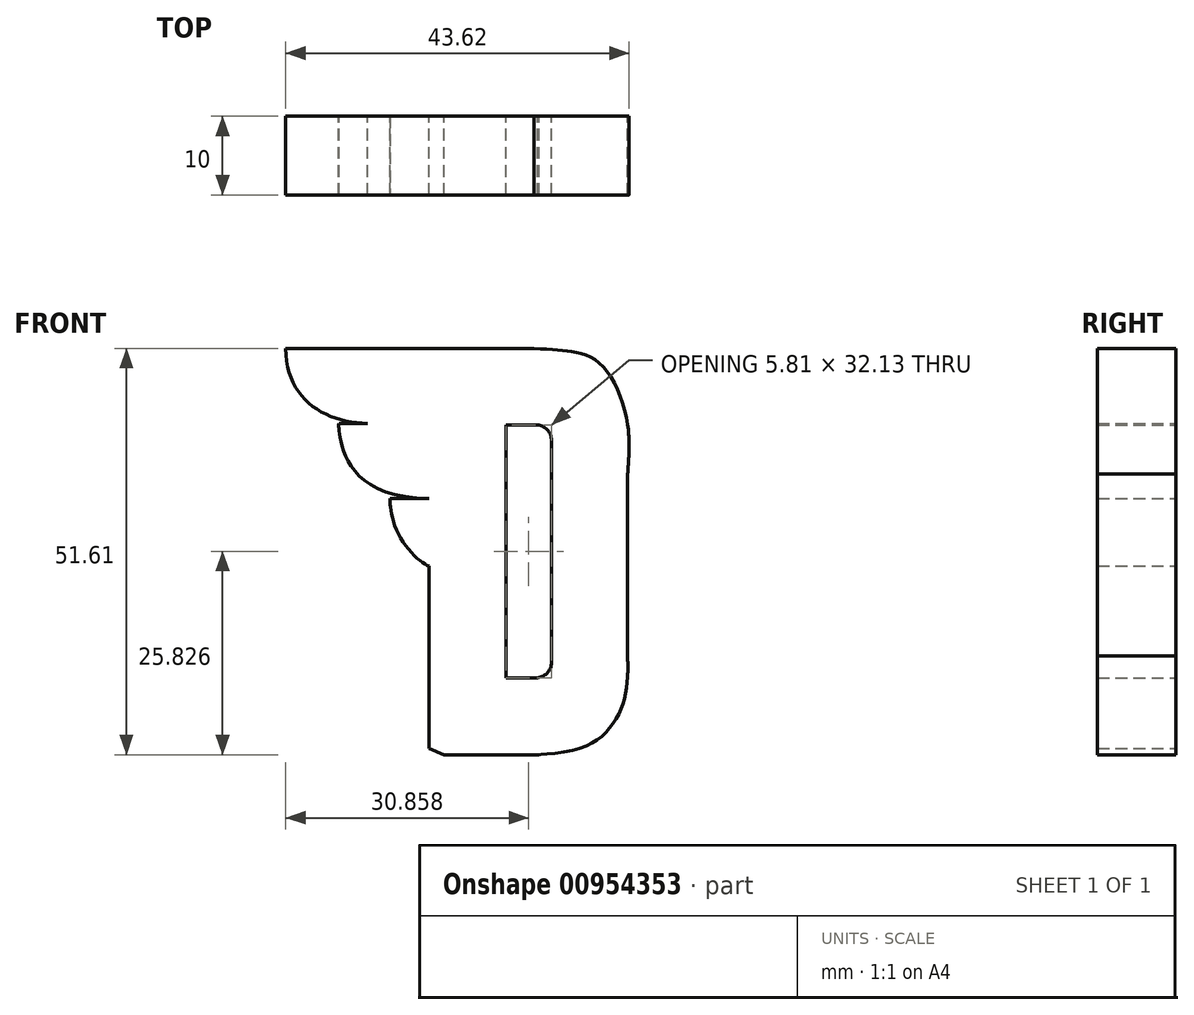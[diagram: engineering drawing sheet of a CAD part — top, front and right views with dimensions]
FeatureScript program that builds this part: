
annotation { "Feature Type Name" : "Feature", "Feature Type Description" : "" }
export const myFeature = defineFeature(function(context is Context, id is Id, definition is map)
    precondition{}
    {
        {
            var Q0;
            Q0=qCreatedBy(makeId("Front.planeOp"),FACE);
            var sketch = newSketch(context, id + "F0", { "sketchPlane" : qUnion([Q0])});
            skLineSegment(sketch, "E0", {"start": v(-33.11, 39.73) * mm, "end": v(-1.57, 39.73) * mm});
            skLineSegment(sketch, "E1", {"start": v(10.32, 30.06) * mm, "end": v(10.32, -2) * mm});
            skFitSpline(sketch, "E2", {"points": [v(-1.57, 39.73) * mm, v(3.32, 39.32) * mm, v(7.13, 37.5) * mm, v(10.32, 30.06) * mm, v(10.32, 23.8) * mm], "startDerivative": vector(27.64, -1.84) * mm, "endDerivative": vector(-1.43, -19.7) * mm});
            skLineSegment(sketch, "E3", {"start": v(-14.92, -11.09) * mm, "end": v(-13.02, -11.88) * mm});
            skLineSegment(sketch, "E4", {"start": v(-13.02, -11.88) * mm, "end": v(-0.96, -11.88) * mm});
            skFitSpline(sketch, "E5", {"points": [v(-0.96, -11.88) * mm, v(2.62, -11.5) * mm, v(7.54, -9.07) * mm, v(9.61, -5.77) * mm, v(10.32, -2) * mm, v(10.32, 0.66) * mm, v(10.32, 0.83) * mm], "startDerivative": vector(-13.72, 0) * mm, "endDerivative": vector(0.1, 2.52) * mm});
            skLineSegment(sketch, "E6", {"start": v(-14.92, -11.09) * mm, "end": v(-14.92, 12.1) * mm});
            skLineSegment(sketch, "E7", {"start": v(-14.9, 20.67) * mm, "end": v(-19.85, 20.67) * mm});
            skLineSegment(sketch, "E8", {"start": v(-22.7, 30.2) * mm, "end": v(-26.36, 30.2) * mm});
            skFitSpline(sketch, "E9", {"points": [v(-14.92, 12.1) * mm, v(-16.37, 13.04) * mm, v(-18.95, 16.47) * mm, v(-19.8, 19.67) * mm, v(-19.85, 20.67) * mm], "startDerivative": vector(-4.8, 1.49) * mm, "endDerivative": vector(0.82, 3.63) * mm});
            skFitSpline(sketch, "E10", {"points": [v(-26.36, 30.2) * mm, v(-26.36, 29.56) * mm, v(-14.9, 20.67) * mm], "startDerivative": vector(-1.22, -3.12) * mm, "endDerivative": vector(38.91, 0) * mm});
            skFitSpline(sketch, "E11", {"points": [v(-33.11, 39.73) * mm, v(-22.73, 30.2) * mm, v(-22.7, 30.2) * mm], "startDerivative": vector(0.13, -20.19) * mm, "endDerivative": vector(-32.01, 0) * mm});
            skLineSegment(sketch, "E12.bottom", {"start": v(-5.16, -2.12) * mm, "end": v(0.65, -2.12) * mm});
            skLineSegment(sketch, "E12.top", {"start": v(-5.16, 30.01) * mm, "end": v(0.65, 30.01) * mm});
            skLineSegment(sketch, "E12.left", {"start": v(-5.16, -2.12) * mm, "end": v(-5.16, 30.01) * mm});
            skLineSegment(sketch, "E12.right", {"start": v(0.65, -2.12) * mm, "end": v(0.65, 30.01) * mm});
            skSolve(sketch);
        }
        {
            var Q0;
            Q0 = qSketchRegion(id + "F0", true);
            extrude(context, id + "F1", {"entities" : qUnion([Q0]), "depth" : 10 * mm, "offsetDistance" : 25 * mm});
        }
        {
            var Q0;
            Q0=makeQuery(id+"F1.opExtrude","SWEPT_EDGE",EDGE,{"disambiguationData":[OSD([sQuery(id+"F0.wireOp",EDGE,"E12.top"),sQuery(id+"F0.wireOp",EDGE,"E12.right")])]});
            fillet(context, id + "F2", {"entities" : qUnion([Q0]), "radius" : 2 * mm, "tangentPropagation" : true, "allowEdgeOverflow" : false});
        }
        {
            var Q0;
            Q0=makeQuery(id+"F1.opExtrude","SWEPT_EDGE",EDGE,{"disambiguationData":[OSD([sQuery(id+"F0.wireOp",EDGE,"E12.bottom"),sQuery(id+"F0.wireOp",EDGE,"E12.right")])]});
            fillet(context, id + "F3", {"entities" : qUnion([Q0]), "radius" : 2 * mm, "tangentPropagation" : true, "allowEdgeOverflow" : false});
        }
    });
